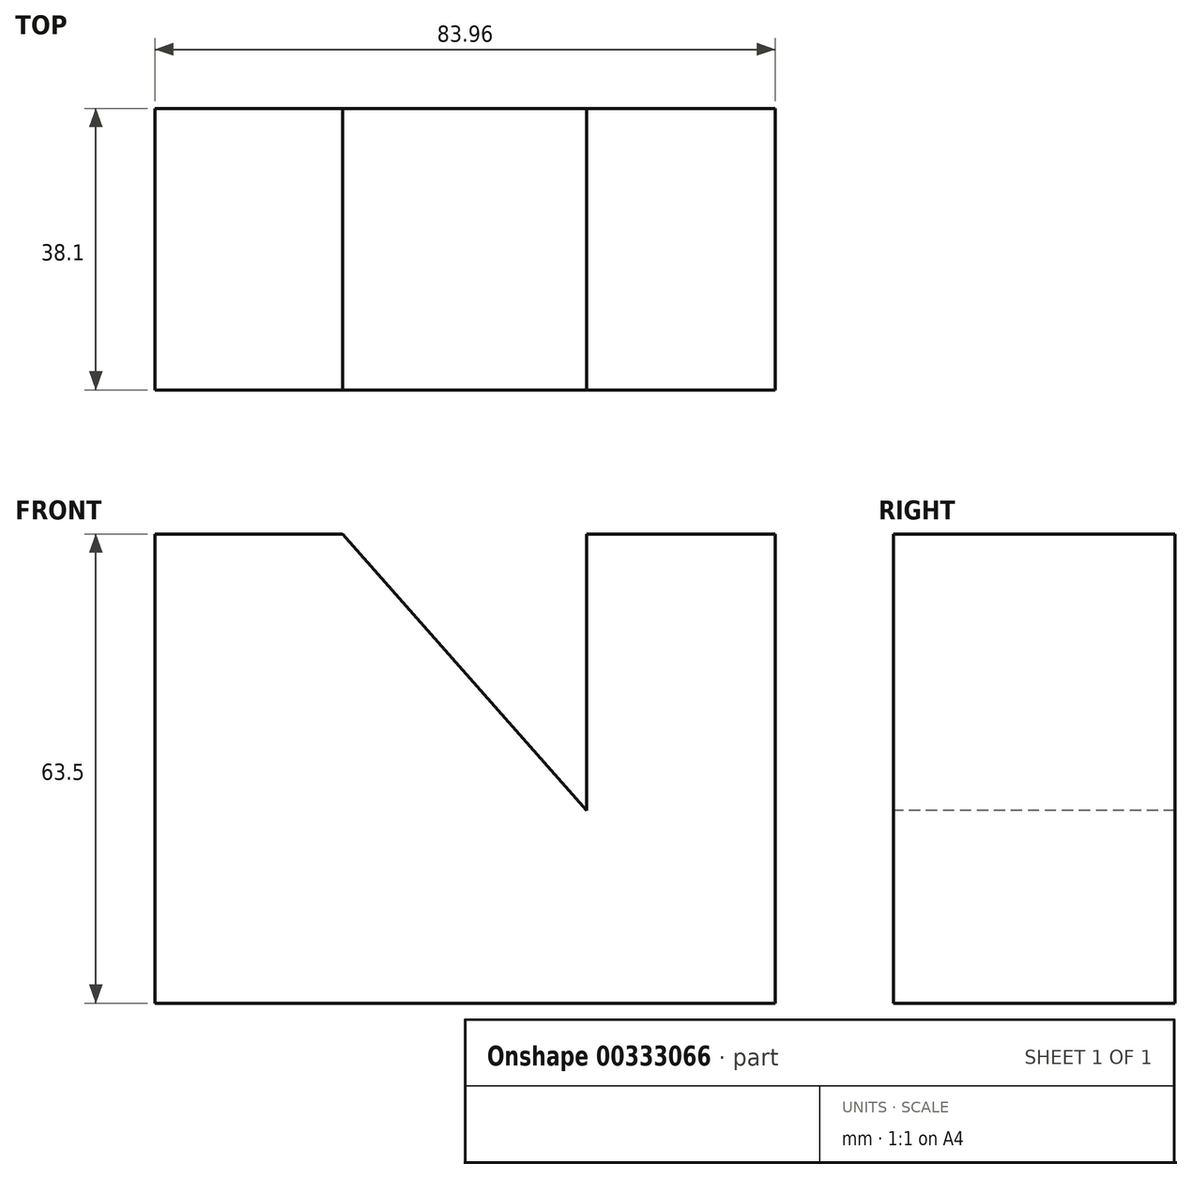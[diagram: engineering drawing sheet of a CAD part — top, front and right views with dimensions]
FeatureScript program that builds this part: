
annotation { "Feature Type Name" : "Feature", "Feature Type Description" : "" }
export const myFeature = defineFeature(function(context is Context, id is Id, definition is map)
    precondition{}
    {
        {
            var Q0;
            Q0=qCreatedBy(makeId("Front.planeOp"),FACE);
            var sketch = newSketch(context, id + "F0", { "sketchPlane" : qUnion([Q0])});
            skLineSegment(sketch, "E0", {"start": v(-32.7, -35.13) * mm, "end": v(26.3, -35.13) * mm});
            skLineSegment(sketch, "E1", {"start": v(26.3, -35.13) * mm, "end": v(26.3, -9.73) * mm});
            skLineSegment(sketch, "E2", {"start": v(26.3, -9.73) * mm, "end": v(-7.3, 28.37) * mm});
            skLineSegment(sketch, "E3", {"start": v(-7.3, 28.37) * mm, "end": v(-32.7, 28.37) * mm});
            skLineSegment(sketch, "E4", {"start": v(-32.7, 28.37) * mm, "end": v(-32.7, -35.13) * mm});
            skSolve(sketch);
        }
        {
            var Q0;
            Q0=makeQuery(id+"F0.imprint","IMPRINT",FACE,{"disambiguationData":[TD([[makeQuery(id+"F0.imprint","IMPRINT",EDGE,{"derivedFrom":sQuery(id+"F0.wireOp",EDGE,"E0")}),1.0]])]});
            extrude(context, id + "F1", {"entities" : qUnion([Q0]), "depth" : 38.1 * mm});
        }
        {
            var Q0;
            Q0=makeQuery(id+"F1.opExtrude","SWEPT_FACE",FACE,{"disambiguationData":[OSD([sQuery(id+"F0.wireOp",EDGE,"E3")])]});
            var sketch = newSketch(context, id + "F2", { "sketchPlane" : qUnion([Q0])});
            skLineSegment(sketch, "E5", {"start": v(25.73, 0) * mm, "end": v(51.27, 0) * mm});
            skLineSegment(sketch, "E6", {"start": v(51.27, 0) * mm, "end": v(51.27, -38.1) * mm});
            skLineSegment(sketch, "E7", {"start": v(51.27, -38.1) * mm, "end": v(25.73, -38.1) * mm});
            skLineSegment(sketch, "E8", {"start": v(25.73, -38.1) * mm, "end": v(25.73, 0) * mm});
            skSolve(sketch);
        }
        {
            var Q0;
            Q0=makeQuery(id+"F2.imprint","IMPRINT",FACE,{"disambiguationData":[TD([[makeQuery(id+"F2.imprint","IMPRINT",EDGE,{"derivedFrom":sQuery(id+"F2.wireOp",EDGE,"E5")}),-1.0]])]});
            extrude(context, id + "F3", {"entities" : qUnion([Q0]), "operationType" : NewBodyOperationType.ADD, "oppositeDirection" : true, "depth" : 63.5 * mm});
        }
    });
